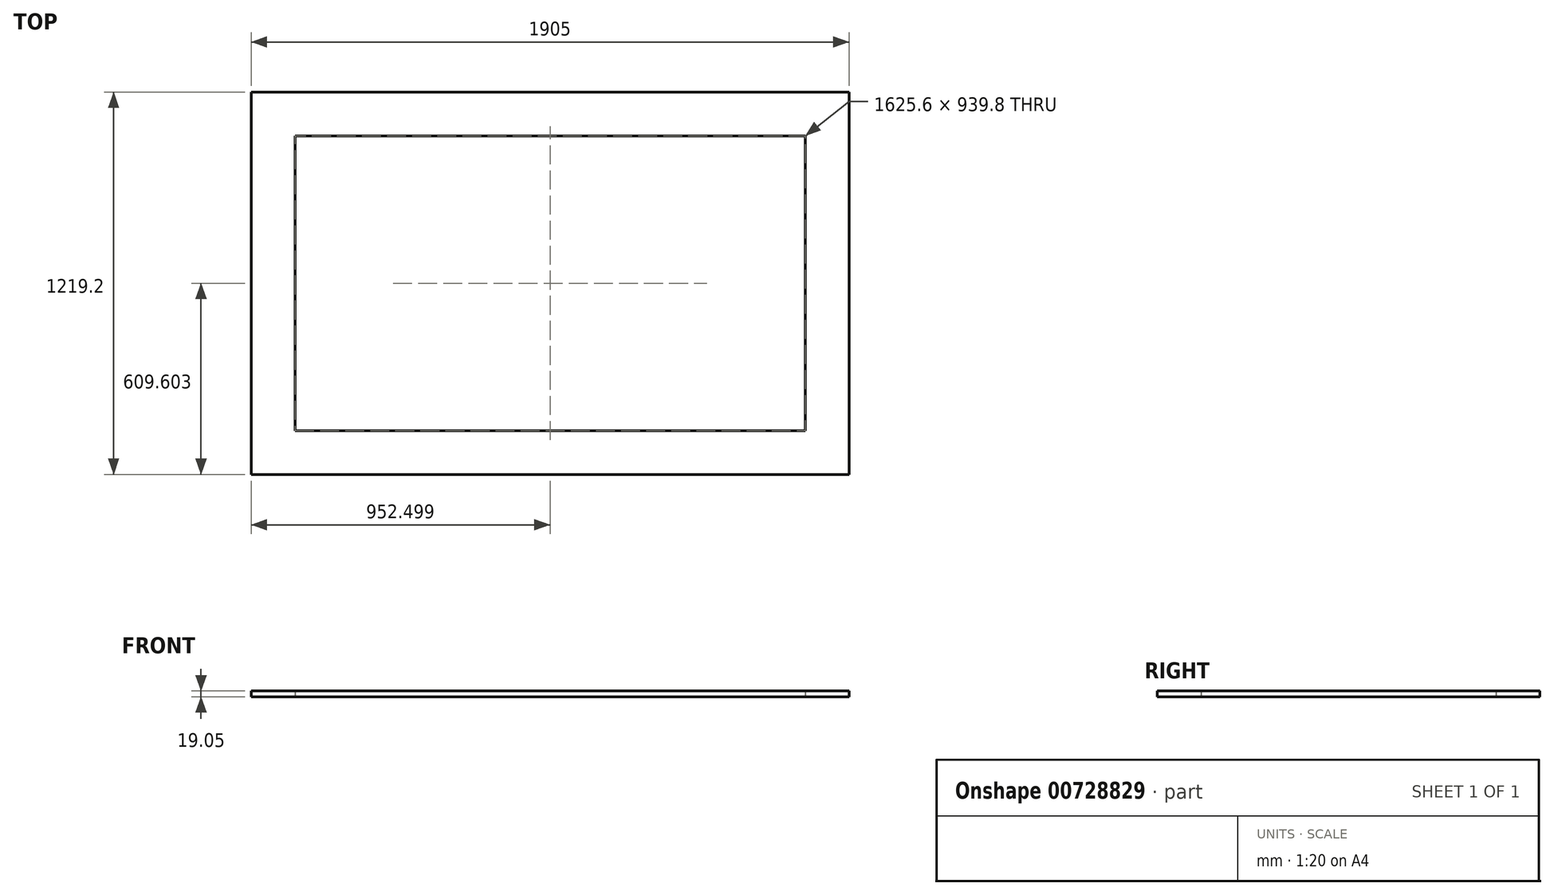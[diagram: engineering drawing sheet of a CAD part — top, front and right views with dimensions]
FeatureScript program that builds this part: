
annotation { "Feature Type Name" : "Feature", "Feature Type Description" : "" }
export const myFeature = defineFeature(function(context is Context, id is Id, definition is map)
    precondition{}
    {
        {
            var Q0;
            Q0=qCreatedBy(makeId("Top.planeOp"),FACE);
            var sketch = newSketch(context, id + "F0", { "sketchPlane" : qUnion([Q0])});
            skLineSegment(sketch, "E0.bottom", {"start": v(-939.15, 835.92) * mm, "end": v(965.85, 835.92) * mm});
            skLineSegment(sketch, "E0.top", {"start": v(-939.15, -383.28) * mm, "end": v(965.85, -383.28) * mm});
            skLineSegment(sketch, "E0.left", {"start": v(-939.15, 835.92) * mm, "end": v(-939.15, -383.28) * mm});
            skLineSegment(sketch, "E0.right", {"start": v(965.85, 835.92) * mm, "end": v(965.85, -383.28) * mm});
            skLineSegment(sketch, "E1.bottom", {"start": v(-799.45, 696.22) * mm, "end": v(826.15, 696.22) * mm});
            skLineSegment(sketch, "E1.top", {"start": v(-799.45, -243.58) * mm, "end": v(826.15, -243.58) * mm});
            skLineSegment(sketch, "E1.left", {"start": v(-799.45, 696.22) * mm, "end": v(-799.45, -243.58) * mm});
            skLineSegment(sketch, "E1.right", {"start": v(826.15, 696.22) * mm, "end": v(826.15, -243.58) * mm});
            skSolve(sketch);
        }
        {
            var Q0;
            Q0=makeQuery(id+"F0.imprint","IMPRINT",FACE,{"disambiguationData":[TD([[makeQuery(id+"F0.imprint","IMPRINT",EDGE,{"derivedFrom":sQuery(id+"F0.wireOp",EDGE,"E0.bottom")}),-1.0]])]});
            extrude(context, id + "F1", {"entities" : qUnion([Q0]), "depth" : 19.05 * mm, "offsetDistance" : 25.4 * mm});
        }
    });
